# Revit family: ASH_Contour21_S0430_BIM_GB
name_source: partatom
category: Plumbing Fixtures
revit_build: Autodesk Revit MEP 2014 (Build: 20130308_1515(x64)
units: mm (PartAtom-declared; Revit-internal decimal feet)

## types (1)
- S0430HY - Contour 21+ 500mm anti-splash back outlet basin - no tapholes - hygenic+ glaze
    Accessories = www.idealspec.co.uk
    AreaUnits = millimeters
    Assembly Code = C1030200
    AssetType = Fixed
    BIMObjectName = ASH_ArmitageShanks_HealthCareClinicalWashBasins_Contour 21+_S0430HY
    Brand = Armitage Shanks
    CWFU = 0
    Color = White
    ConnectionType = Plumbing
    Cost = 0 $
    Default Elevation = 850 mm  [stored 2.78871 ft]
    Description = Contour 21+ 50cm back outlet washbasin no tapholes anti-splash, anti-bacterial glaze
    DrainSize = 0 mm  [stored 0 ft]
    DurationUnit = year
    ECA = No
    ExpectedLife = 30
    Features = 50cm back outlet washbasin no tapholes anti-splash, anti-bacterial glaze
    Finish = White
    HWFU = 0
    Help = www.idealspec.co.uk/contact-us.html
    IfcExportAs = IfcSanitaryType
    IfcExportType = WASHHANDBASIN
    InstallationInstructions = www.idealspec.co.uk/resources.html
    LinearUnits = millimeters
    ManufacturerURL = www.idealspec.co.uk
    Material = Vitreous china
    Model = S0430HY
    ModelNumber = S0430HY
    ModelReference = Contour 21+ 50cm back outlet washbasin no tapholes anti-splash, anti-bacterial glaze
    NBSDescription = Health care clinical wash basins
    NBSReference = 45-35-70/361
    Name = HealthCareClinicalWashBasins_Contour 21+_S0430HY_ArmitageShanks
    NettWeight = 13 Kg
    NominalDepth = 400 mm  [stored 1.31234 ft]
    NominalHeight = 200 mm  [stored 0.656168 ft]
    NominalLength = 500 mm  [stored 1.64042 ft]
    NominalWidth = 500 mm  [stored 1.64042 ft]
    ProductInformation = www.idealspec.co.uk
    Shape = Sculptured
    Size = 400 x 500 x 200 mm
    Space = Internal
    URL = www.idealspec.co.uk
    Uniclass2015Code = Pr_40_20_96_95
    Uniclass2015Title = Wall-hung hand rinse basins
    Uniclass2015Version = Product v1.1
    Version = 1
    VolumeUnits = Litres
    WFU = 0
    WRAS = No
    WarrantyDescription = Manufacturers Warranty
    WarrantyDurationParts = 99
    WarrantyDurationUnit = year
    WashHandBasinMounting = Wall only
    WashHandBasinType = Hand Rinse
    WaterEfficientProduct = No

note: [stored X ft] marks values corroborated as IEEE doubles in the binary element streams (Revit-internal decimal feet)

## geometry (parser evidence)
native form markers: Sweep x2
no freeform markers — native parametric forms only
